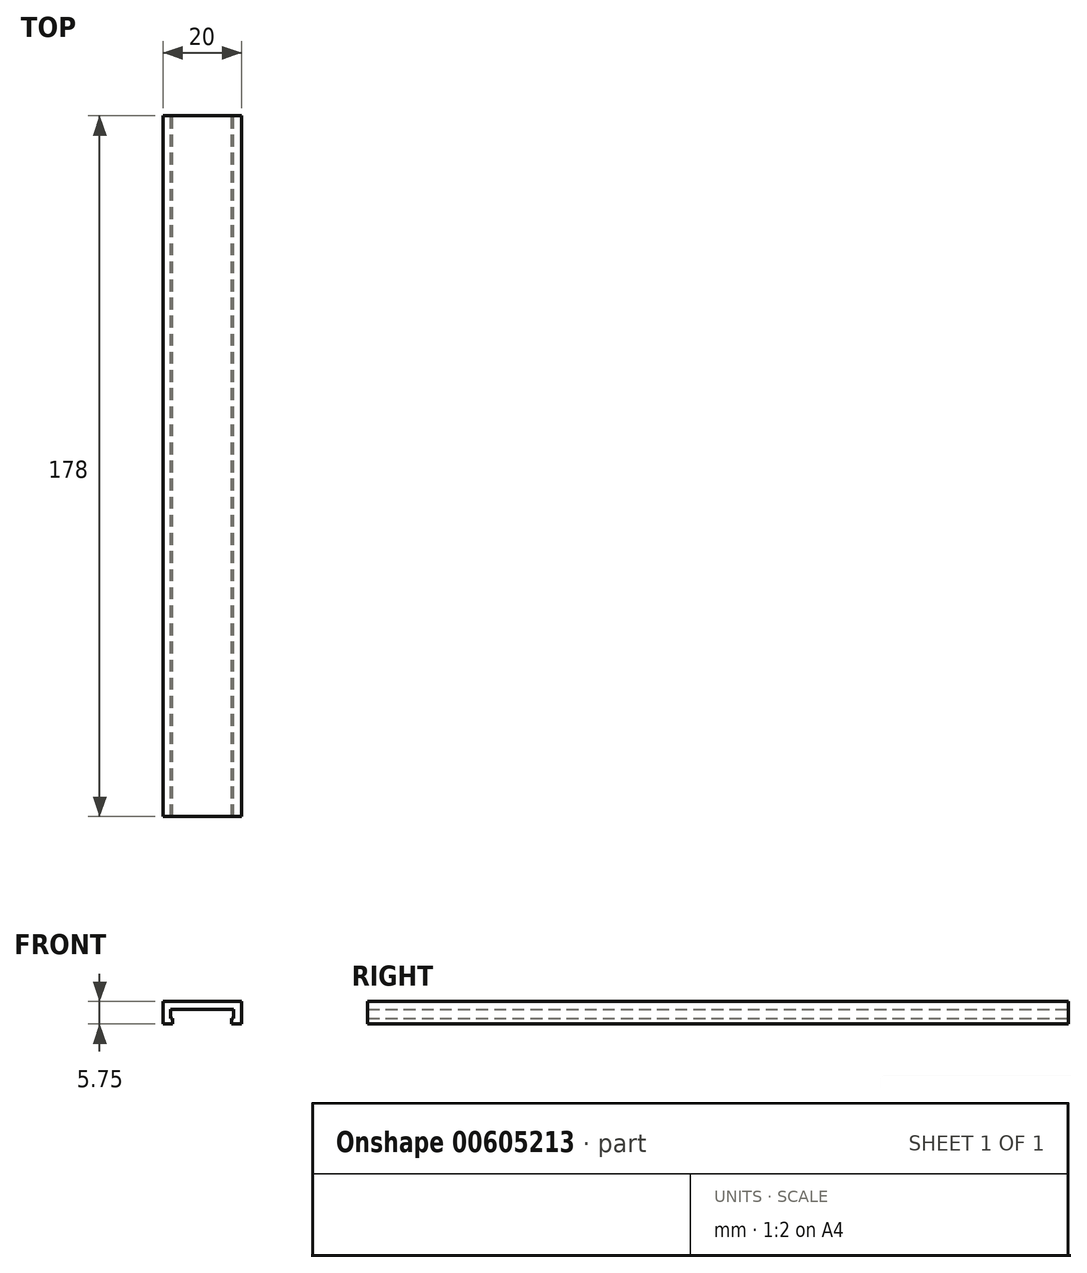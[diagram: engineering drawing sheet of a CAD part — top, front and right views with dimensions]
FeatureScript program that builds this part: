
annotation { "Feature Type Name" : "Feature", "Feature Type Description" : "" }
export const myFeature = defineFeature(function(context is Context, id is Id, definition is map)
    precondition{}
    {
        {
            var Q0;
            Q0=qCreatedBy(makeId("Front.planeOp"),FACE);
            var sketch = newSketch(context, id + "F0", { "sketchPlane" : qUnion([Q0])});
            skLineSegment(sketch, "E0", {"start": v(0, 0) * mm, "end": v(10, 0) * mm});
            skLineSegment(sketch, "E1", {"start": v(10, 0) * mm, "end": v(10, -5.75) * mm});
            skLineSegment(sketch, "E2", {"start": v(10, -5.75) * mm, "end": v(7.5, -5.75) * mm});
            skLineSegment(sketch, "E3", {"start": v(7.5, -5.75) * mm, "end": v(7.5, -4.25) * mm});
            skLineSegment(sketch, "E4", {"start": v(7.5, -4.25) * mm, "end": v(8, -4.25) * mm});
            skLineSegment(sketch, "E5", {"start": v(8, -4.25) * mm, "end": v(8, -2) * mm});
            skLineSegment(sketch, "E6", {"start": v(8, -2) * mm, "end": v(0, -2) * mm});
            skLineSegment(sketch, "E7", {"start": v(0, -2) * mm, "end": v(0, 0) * mm});
            skSolve(sketch);
        }
        {
            var Q0;
            Q0=makeQuery(id+"F0.imprint","IMPRINT",FACE,{"disambiguationData":[TD([[makeQuery(id+"F0.imprint","IMPRINT",EDGE,{"derivedFrom":sQuery(id+"F0.wireOp",EDGE,"E0")}),-1.0]])]});
            extrude(context, id + "F1", {"entities" : qUnion([Q0]), "depth" : 178 * mm, "offsetDistance" : 25 * mm});
        }
        {
            var Q0;
            Q0=makeQuery(id+"F1.opExtrude","SWEPT_BODY",BODY,{"disambiguationData":[OSD([sQuery(id+"F0.wireOp",EDGE,"E0"),sQuery(id+"F0.wireOp",EDGE,"E1"),sQuery(id+"F0.wireOp",EDGE,"E2"),sQuery(id+"F0.wireOp",EDGE,"E3"),sQuery(id+"F0.wireOp",EDGE,"E4"),sQuery(id+"F0.wireOp",EDGE,"E5"),sQuery(id+"F0.wireOp",EDGE,"E6"),sQuery(id+"F0.wireOp",EDGE,"E7")])]});
            var Q1;
            Q1=qCreatedBy(makeId("Right.planeOp"),FACE);
            mirror(context, id + "F2", {"operationType" : NewBodyOperationType.ADD, "entities" : qUnion([Q0]), "mirrorPlane" : qUnion([Q1])});
        }
    });
